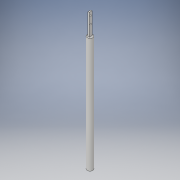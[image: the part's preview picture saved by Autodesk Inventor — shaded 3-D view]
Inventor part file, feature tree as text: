
AUTODESK INVENTOR PART (.ipt)
format: ipt  version: 2017 (Build 210142000, 142)  size: 112,640 bytes
history: native  units: in
note: dims shown in document units (in); Inventor stores cm internally (conversion verified against a paired STEP export)
features: sketch x3, extrude x2, hole x1
ambient origin geometry x8: Origin, YZ Plane, XZ Plane, XY Plane, X Axis, Y Axis, Z Axis, Center Point
bodies: Solid1 (feature_tree)
feature tree (6):
  extrude  "Extrusion1"  Depth=6.2992in TaperAngle=0.0deg
  extrude  "Extrusion2"  Depth=0.0709in
  hole  "Hole1"  [1 undecoded]
  sketch  "Sketch1"  dims[d0=0.311in d1=6.2992in d2=0.0in]
  sketch  "Sketch2"  dims[d3=0.1496in d4=0.0709in]
  sketch  "Sketch3"  dims[d5=1.1811in d6=0.0in d7=0.1969in d8=0.0866in d9=0.3937in d10=0.0866in d11=0.0787in d12=0.2362in d13=0.1575in d14=0.0787in d15=90.0deg d16=0.315in d17=0.8108in]
note: 1 required parameter value undecoded (feature->parameter linkage not recoverable at this tier; creation-order binding heuristic only, values carry confidence <= 0.55)
